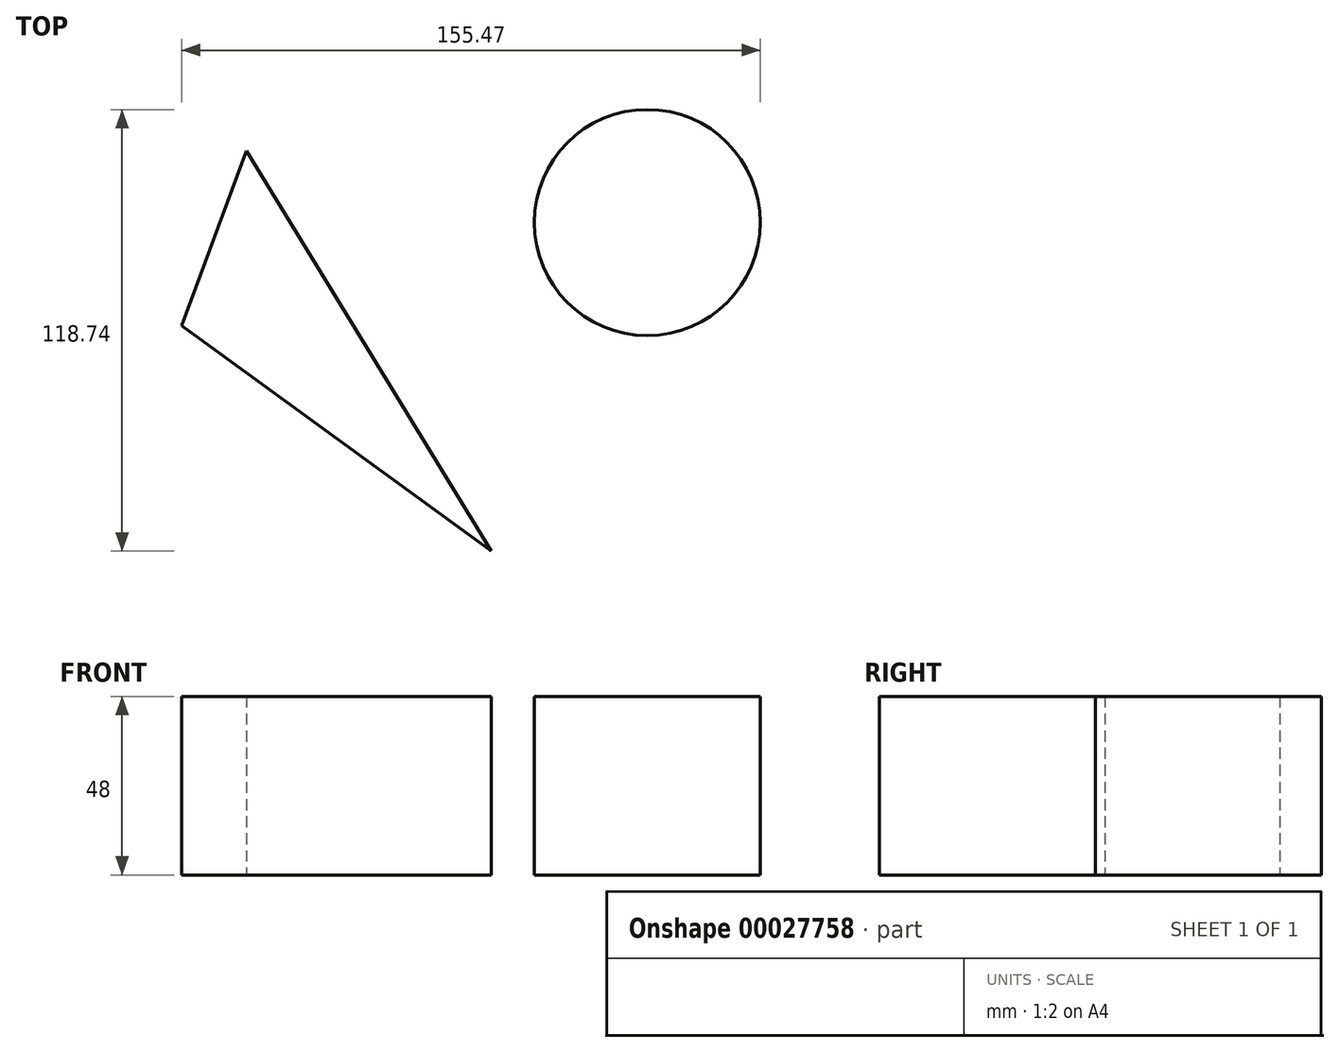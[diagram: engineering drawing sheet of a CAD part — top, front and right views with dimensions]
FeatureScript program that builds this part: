
annotation { "Feature Type Name" : "Feature", "Feature Type Description" : "" }
export const myFeature = defineFeature(function(context is Context, id is Id, definition is map)
    precondition{}
    {
        {
            var Q0;
            Q0=qCreatedBy(makeId("Top.planeOp"),FACE);
            var sketch = newSketch(context, id + "F0", { "sketchPlane" : qUnion([Q0])});
            skLineSegment(sketch, "E0", {"start": v(-134.74, 0) * mm, "end": v(-117.39, 46.97) * mm});
            skLineSegment(sketch, "E1", {"start": v(-117.39, 46.97) * mm, "end": v(-51.57, -60.62) * mm});
            skLineSegment(sketch, "E2", {"start": v(-51.57, -60.62) * mm, "end": v(-134.74, 0) * mm});
            skCircle(sketch, "E3", {"center": v(-9.64, 27.74) * mm, "radius": 30.37 * mm});
            skSolve(sketch);
        }
        {
            var Q0;
            Q0 = qSketchRegion(id + "F0", true);
            extrude(context, id + "F1", {"entities" : qUnion([Q0]), "depth" : 48 * mm});
        }
    });
